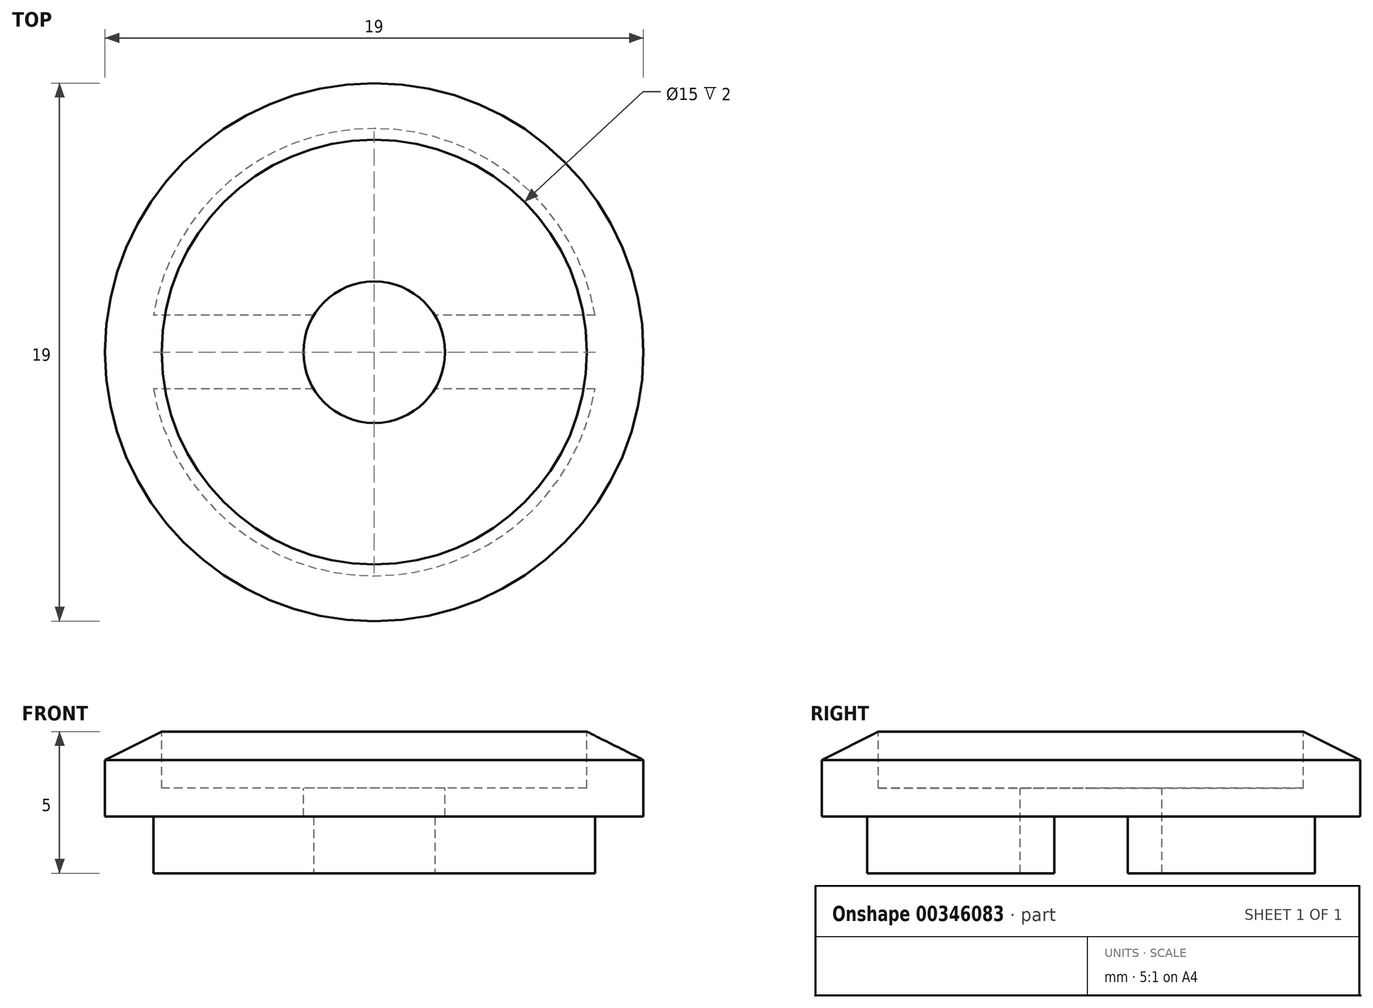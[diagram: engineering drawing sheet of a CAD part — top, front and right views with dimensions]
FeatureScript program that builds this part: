
annotation { "Feature Type Name" : "Feature", "Feature Type Description" : "" }
export const myFeature = defineFeature(function(context is Context, id is Id, definition is map)
    precondition{}
    {
        {
            var Q0;
            Q0=qCreatedBy(makeId("Front.planeOp"),FACE);
            var sketch = newSketch(context, id + "F0", { "sketchPlane" : qUnion([Q0])});
            skLineSegment(sketch, "E0", {"start": v(2.5, -0.31) * mm, "end": v(9.5, -0.31) * mm});
            skLineSegment(sketch, "E1", {"start": v(9.5, -0.31) * mm, "end": v(9.5, 1.69) * mm});
            skLineSegment(sketch, "E2", {"start": v(9.5, 1.69) * mm, "end": v(7.5, 2.69) * mm});
            skLineSegment(sketch, "E3", {"start": v(7.5, 2.69) * mm, "end": v(7.5, 2.69) * mm});
            skLineSegment(sketch, "E4", {"start": v(7.5, 2.69) * mm, "end": v(2.5, 2.69) * mm});
            skLineSegment(sketch, "E5", {"start": v(2.5, 2.69) * mm, "end": v(2.5, -0.31) * mm});
            skLineSegment(sketch, "E6", {"start": v(2.5, 2.69) * mm, "end": v(0, 2.69) * mm});
            skLineSegment(sketch, "E7", {"start": v(0, 2.69) * mm, "end": v(0, -0.31) * mm});
            skLineSegment(sketch, "E8", {"start": v(0, -0.31) * mm, "end": v(2.5, -0.31) * mm});
            skSolve(sketch);
        }
        {
            var Q0;
            Q0=makeQuery(id+"F0.imprint","IMPRINT",FACE,{"disambiguationData":[TD([[makeQuery(id+"F0.imprint","IMPRINT",EDGE,{"derivedFrom":sQuery(id+"F0.wireOp",EDGE,"E0")}),1.0]])]});
            var Q1;
            Q1=sQuery(id+"F0.wireOp",EDGE,"E7");
            revolve(context, id + "F1", {"entities" : qUnion([Q0]), "axis" : qUnion([Q1]), "revolveType" : RevolveType.FULL});
        }
        {
            var Q0;
            Q0=makeQuery(id+"F1.opRevolve","SWEPT_FACE",FACE,{"disambiguationData":[OSD([sQuery(id+"F0.wireOp",EDGE,"E0")])]});
            var sketch = newSketch(context, id + "F2", { "sketchPlane" : qUnion([Q0])});
            skCircle(sketch, "E9", {"center": v(0, 0) * mm, "radius": 7.9 * mm});
            skSolve(sketch);
        }
        {
            var Q0;
            Q0=qSketchRegion(id+"F2",true);
            extrude(context, id + "F3", {"entities" : qUnion([Q0]), "operationType" : NewBodyOperationType.ADD, "depth" : 2 * mm});
        }
        {
            var Q0;
            Q0=makeQuery(id+"F3.opExtrude","CAP_FACE",FACE,{"disambiguationData":[OSD([sQuery(id+"F2.wireOp",EDGE,"E9")])],"isStart":false});
            var sketch = newSketch(context, id + "F4", { "sketchPlane" : qUnion([Q0])});
            skCircle(sketch, "E10", {"center": v(0, 0) * mm, "radius": 2.5 * mm});
            skLineSegment(sketch, "E11.bottom", {"start": v(8.27, -1.3) * mm, "end": v(-8.27, -1.3) * mm});
            skLineSegment(sketch, "E11.top", {"start": v(8.27, 1.3) * mm, "end": v(-8.27, 1.3) * mm});
            skLineSegment(sketch, "E11.left", {"start": v(8.27, -1.3) * mm, "end": v(8.27, 1.3) * mm});
            skLineSegment(sketch, "E11.right", {"start": v(-8.27, -1.3) * mm, "end": v(-8.27, 1.3) * mm});
            skSolve(sketch);
        }
        {
            var Q0;
            Q0=qSketchRegion(id+"F4",true);
            extrude(context, id + "F5", {"entities" : qUnion([Q0]), "operationType" : NewBodyOperationType.REMOVE, "oppositeDirection" : true, "depth" : 2 * mm});
        }
        {
            var Q0;
            Q0=makeQuery(id+"F1.opRevolve","SWEPT_FACE",FACE,{"disambiguationData":[OSD([sQuery(id+"F0.wireOp",EDGE,"E4")])]});
            var sketch = newSketch(context, id + "F6", { "sketchPlane" : qUnion([Q0])});
            skCircle(sketch, "E12", {"center": v(0, 0) * mm, "radius": 7.5 * mm});
            skSolve(sketch);
        }
        {
            var Q0;
            Q0=qSketchRegion(id+"F6",true);
            extrude(context, id + "F7", {"entities" : qUnion([Q0]), "operationType" : NewBodyOperationType.REMOVE, "oppositeDirection" : true, "depth" : 2 * mm});
        }
        {
            var Q0;
            Q0 = qSketchRegion(id + "F6", true);
            extrude(context, id + "F8", {"entities" : qUnion([Q0]), "operationType" : NewBodyOperationType.REMOVE, "oppositeDirection" : true, "depth" : 1 * mm});
        }
    });
